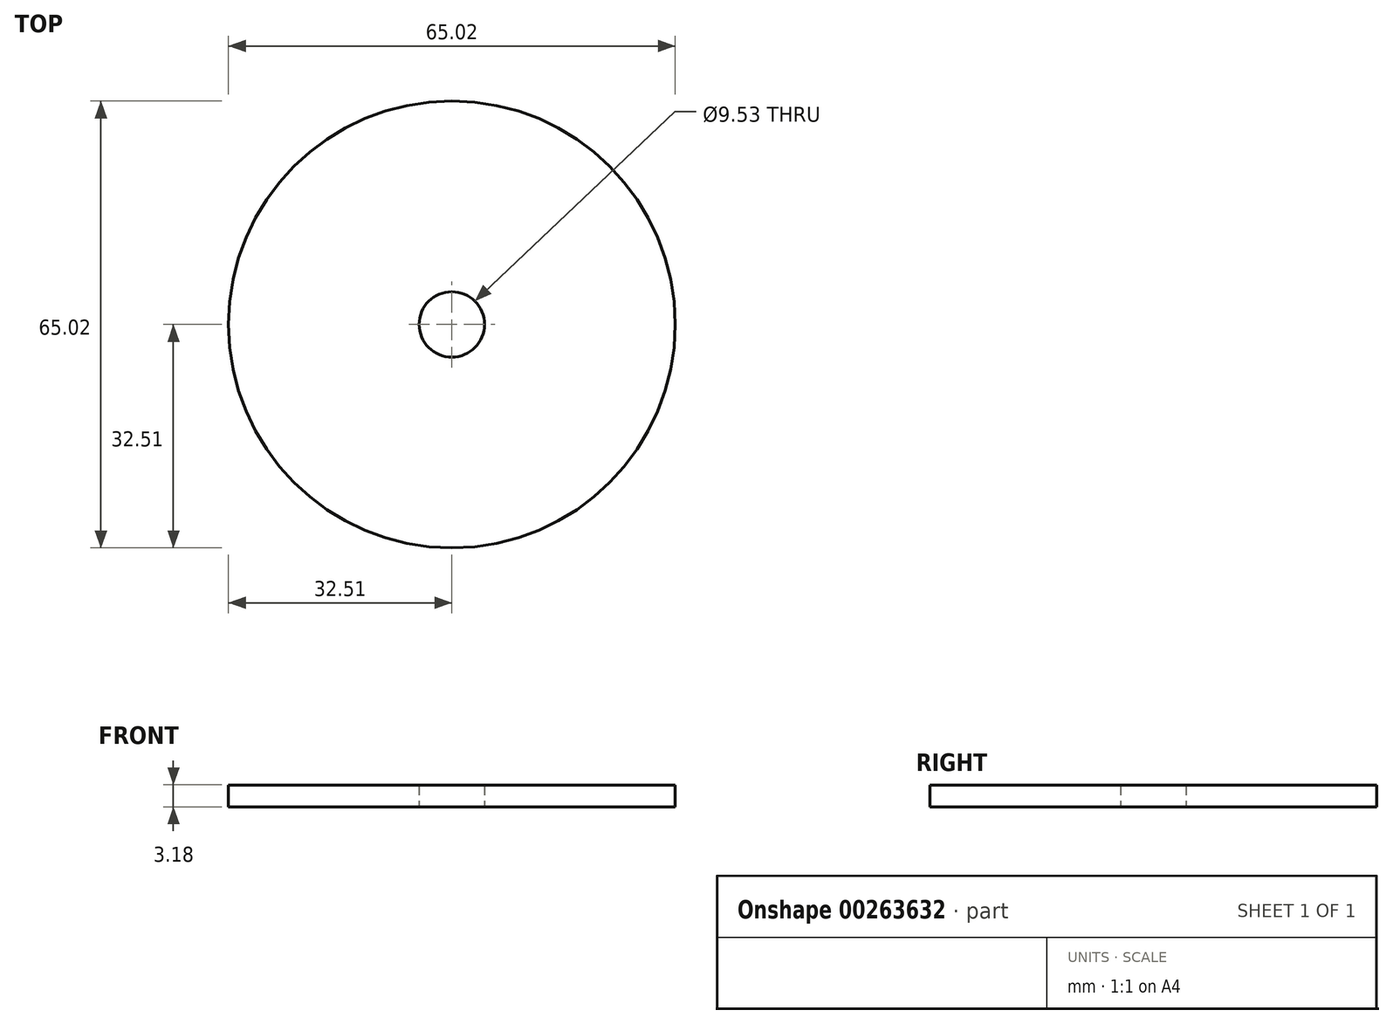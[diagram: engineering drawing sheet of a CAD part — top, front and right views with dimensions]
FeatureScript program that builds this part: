
annotation { "Feature Type Name" : "Feature", "Feature Type Description" : "" }
export const myFeature = defineFeature(function(context is Context, id is Id, definition is map)
    precondition{}
    {
        {
            var Q0;
            Q0=qCreatedBy(makeId("Top.planeOp"),FACE);
            var sketch = newSketch(context, id + "F0", { "sketchPlane" : qUnion([Q0])});
            skCircle(sketch, "E0", {"center": v(0, 0) * mm, "radius": 32.51 * mm});
            skCircle(sketch, "E1", {"center": v(0, 0) * mm, "radius": 4.76 * mm});
            skSolve(sketch);
        }
        {
            var Q0;
            Q0 = qSketchRegion(id + "F0", true);
            extrude(context, id + "F1", {"entities" : qUnion([Q0]), "depth" : 3.17 * mm});
        }
    });
